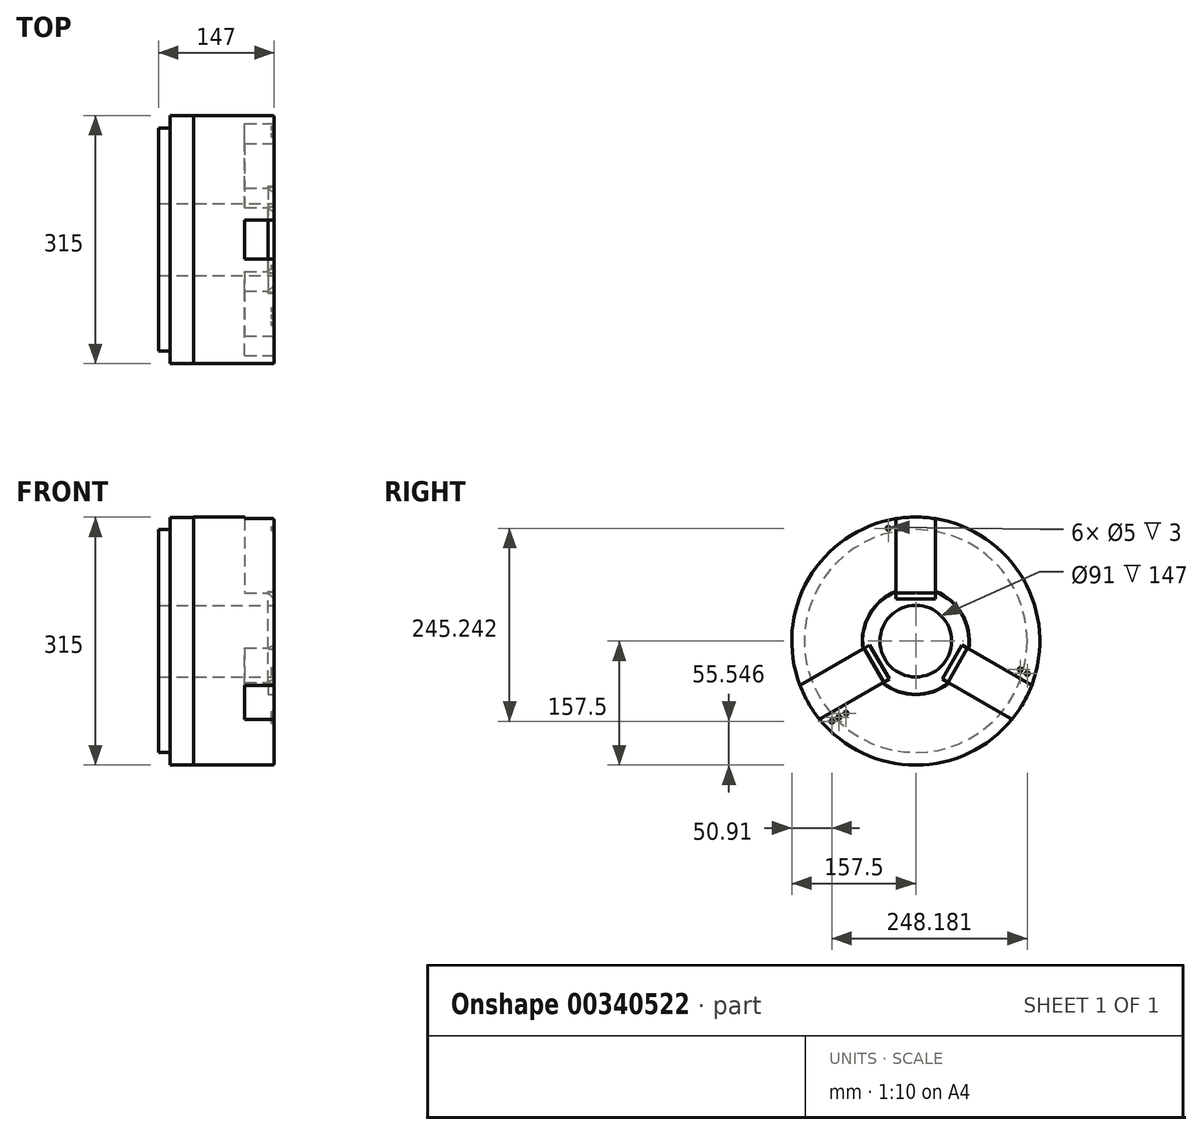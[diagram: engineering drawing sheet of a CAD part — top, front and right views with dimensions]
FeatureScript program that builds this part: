
annotation { "Feature Type Name" : "Feature", "Feature Type Description" : "" }
export const myFeature = defineFeature(function(context is Context, id is Id, definition is map)
    precondition{}
    {
        {
            var Q0;
            Q0=qCreatedBy(makeId("Front.planeOp"),FACE);
            var sketch = newSketch(context, id + "F0", { "sketchPlane" : qUnion([Q0])});
            skLineSegment(sketch, "E0", {"start": v(0, 45.5) * mm, "end": v(0, 67.5) * mm});
            skLineSegment(sketch, "E1", {"start": v(-2, 157.5) * mm, "end": v(-102, 157.5) * mm});
            skLineSegment(sketch, "E2", {"start": v(-132, 157.25) * mm, "end": v(-132, 141.5) * mm});
            skLineSegment(sketch, "E3", {"start": v(-132, 141.5) * mm, "end": v(-147, 141.5) * mm});
            skLineSegment(sketch, "E4", {"start": v(-147, 141.5) * mm, "end": v(-147, 45.5) * mm});
            skLineSegment(sketch, "E5", {"start": v(-147, 45.5) * mm, "end": v(0, 45.5) * mm});
            skLineSegment(sketch, "E6", {"start": v(294.82, 0) * mm, "end": v(-412.28, 0) * mm, "construction": true});
            skPoint(sketch, "E7.visualSharp", {"position": v(0, 157.5) * mm});
            skArc(sketch, "E7.filletArc", {"start": v(0, 155.5) * mm, "mid": v(-0.59, 156.91) * mm, "end": v(-2, 157.5) * mm});
            skLineSegment(sketch, "E8.bottom", {"start": v(0, 67.5) * mm, "end": v(-8, 67.5) * mm});
            skLineSegment(sketch, "E8.top", {"start": v(0, 68) * mm, "end": v(-8, 68) * mm});
            skLineSegment(sketch, "E8.right", {"start": v(-8, 67.5) * mm, "end": v(-8, 68) * mm});
            skLineSegment(sketch, "E9.trimOffspring", {"start": v(0, 68) * mm, "end": v(0, 155.5) * mm});
            skLineSegment(sketch, "E10", {"start": v(-132, 157.25) * mm, "end": v(-102, 157.25) * mm});
            skLineSegment(sketch, "E11", {"start": v(-102, 157.25) * mm, "end": v(-102, 157.5) * mm});
            skPoint(sketch, "E12.orphan", {"position": v(-132, 157.5) * mm});
            skSolve(sketch);
        }
        {
            var Q0;
            Q0=qSketchRegion(id+"F0",true);
            var Q1;
            Q1=sQuery(id+"F0.wireOp",EDGE,"E6");
            revolve(context, id + "F1", {"entities" : qUnion([Q0]), "axis" : qUnion([Q1]), "revolveType" : RevolveType.FULL});
        }
        {
            var Q0;
            Q0=makeQuery(id+"F1.opRevolve","SWEPT_FACE",FACE,{"disambiguationData":[OSD([sQuery(id+"F0.wireOp",EDGE,"E0")])]});
            var sketch = newSketch(context, id + "F2", { "sketchPlane" : qUnion([Q0])});
            skLineSegment(sketch, "E13", {"start": v(0, 0) * mm, "end": v(0, 187.03) * mm, "construction": true});
            skArc(sketch, "E14", {"start": v(25, 155.5) * mm, "mid": v(0, 157.5) * mm, "end": v(-25, 155.5) * mm});
            skPoint(sketch, "E15", {"position": v(0, 62.16) * mm});
            skLineSegment(sketch, "E16", {"start": v(25, 155.5) * mm, "end": v(25, 60.5) * mm});
            skLineSegment(sketch, "E17", {"start": v(25, 60.5) * mm, "end": v(-25, 60.5) * mm});
            skLineSegment(sketch, "E18", {"start": v(-25, 60.5) * mm, "end": v(-25, 155.5) * mm});
            skSolve(sketch);
        }
        {
            var Q0;
            {var subQ0=sQuery(id+"F2.wireOp",EDGE,"E14");Q0=makeQuery(id+"F2.imprint","IMPRINT",FACE,{"disambiguationData":[TD([[makeQuery(id+"F2.imprint","IMPRINT",EDGE,{"derivedFrom":subQ0}),1.0]])]});}
            var Q1;
            {var subQ0=sQuery(id+"F2.wireOp",EDGE,"LmhPQE9t-ctvD-aCPM-Uwr9-EQLkLqq6skGc.bottom");Q1=makeQuery(id+"F2.imprint","IMPRINT",FACE,{"disambiguationData":[TD([[makeQuery(id+"F2.imprint","IMPRINT",EDGE,{"derivedFrom":subQ0}),-1.0]])]});}
            var Q2;
            {var subQ0=sQuery(id+"F2.wireOp",EDGE,"LmhPQE9t-ctvD-aCPM-Uwr9-EQLkLqq6skGc.bottom");var subQ1=makeQuery(id+"F1.opRevolve","SWEPT_EDGE",EDGE,{"disambiguationData":[OSD([sQuery(id+"F0.wireOp",EDGE,"E0"),sQuery(id+"F0.wireOp",EDGE,"E8.bottom")])]});var subQ2=makeQuery(id+"F2.imprint","INTERSECT",VERTEX,{"disambiguationData":[OD(0.0)],"derivedFrom":[subQ1,subQ0]});Q2=makeQuery(id+"F2.imprint","IMPRINT",FACE,{"disambiguationData":[TD([[makeQuery(id+"F2.imprint","IMPRINT",EDGE,{"disambiguationData":[TD([[subQ2,-1.0]])],"derivedFrom":subQ0}),-1.0]])]});}
            extrude(context, id + "F3", {"entities" : qUnion([Q0, Q1, Q2]), "operationType" : NewBodyOperationType.REMOVE, "oppositeDirection" : true, "depth" : 37.5 * mm});
        }
        {
            var Q0;
            Q0=makeQuery(id+"F1.opRevolve","SWEPT_FACE",FACE,{"disambiguationData":[OSD([sQuery(id+"F0.wireOp",EDGE,"E0")])]});
            var sketch = newSketch(context, id + "F4", { "sketchPlane" : qUnion([Q0])});
            skLineSegment(sketch, "E19", {"start": v(25, 73.3) * mm, "end": v(-25, 73.3) * mm});
            skLineSegment(sketch, "E20", {"start": v(-25, 73.3) * mm, "end": v(-25, 53.3) * mm});
            skLineSegment(sketch, "E21", {"start": v(-25, 53.3) * mm, "end": v(25, 53.3) * mm});
            skLineSegment(sketch, "E22", {"start": v(25, 53.3) * mm, "end": v(25, 73.3) * mm});
            skSolve(sketch);
        }
        {
            var Q0;
            Q0=qSketchRegion(id+"F4",true);
            extrude(context, id + "F5", {"entities" : qUnion([Q0]), "operationType" : NewBodyOperationType.REMOVE, "oppositeDirection" : true, "depth" : 8 * mm});
        }
        {
            var Q0;
            Q0=makeQuery(id+"F5.boolean.opBoolean","COPY",EDGE,{"derivedFrom":makeQuery(id+"F5.opExtrude","CAP_EDGE",EDGE,{"disambiguationData":[OSD([sQuery(id+"F4.wireOp",EDGE,"E21")])],"isStart":false})});
            chamfer(context, id + "F6", {"entities" : qUnion([Q0]), "width" : 8 * mm, "tangentPropagation" : true});
        }
        {
            var Q0;
            Q0=makeQuery(id+"F5.boolean.opBoolean","COPY",FACE,{"derivedFrom":makeQuery(id+"F5.opExtrude","CAP_FACE",FACE,{"disambiguationData":[OSD([sQuery(id+"F4.wireOp",EDGE,"E19"),sQuery(id+"F4.wireOp",EDGE,"E20"),sQuery(id+"F4.wireOp",EDGE,"E21"),sQuery(id+"F4.wireOp",EDGE,"E22")])],"isStart":false})});
            var Q1;
            Q1=makeQuery(id+"F3.boolean.opBoolean","COPY",FACE,{"derivedFrom":makeQuery(id+"F3.opExtrude","CAP_FACE",FACE,{"disambiguationData":[OSD([sQuery(id+"F0.wireOp",EDGE,"E0"),sQuery(id+"F0.wireOp",EDGE,"E8.bottom"),sQuery(id+"F2.wireOp",EDGE,"E14"),sQuery(id+"F2.wireOp",EDGE,"E16"),sQuery(id+"F2.wireOp",EDGE,"E18")])],"isStart":false})});
            extrude(context, id + "F7", {"entities" : qUnion([Q0]), "operationType" : NewBodyOperationType.REMOVE, "endBound" : BoundingType.UP_TO_SURFACE, "oppositeDirection" : true, "endBoundEntityFace" : qUnion([Q1]), "depth" : 25 * mm});
        }
        {
            var Q0;
            Q0=makeQuery(id+"F6.opChamfer","BLEND_FACE",FACE,{"disambiguationData":[OSD([sQuery(id+"F4.wireOp",EDGE,"E21")])]});
            var Q1;
            {var subQ0=sQuery(id+"F4.wireOp",EDGE,"E22");Q1=makeQuery(id+"F7.boolean.opBoolean","MERGE",FACE,{"derivedFrom":[makeQuery(id+"F3.boolean.opBoolean","COPY",FACE,{"derivedFrom":makeQuery(id+"F3.opExtrude","SWEPT_FACE",FACE,{"disambiguationData":[OSD([sQuery(id+"F2.wireOp",EDGE,"E16")])]})}),makeQuery(id+"F5.boolean.opBoolean","COPY",FACE,{"derivedFrom":makeQuery(id+"F5.opExtrude","SWEPT_FACE",FACE,{"disambiguationData":[OSD([subQ0])]})}),makeQuery(id+"F7.opExtrude","SWEPT_FACE",FACE,{"disambiguationData":[OSD([subQ0])]})]});}
            var Q2;
            Q2=makeQuery(id+"F7.boolean.opBoolean","COPY",FACE,{"derivedFrom":makeQuery(id+"F7.opExtrude","SWEPT_FACE",FACE,{"disambiguationData":[OSD([sQuery(id+"F4.wireOp",EDGE,"E19"),sQuery(id+"F4.wireOp",EDGE,"E20"),sQuery(id+"F4.wireOp",EDGE,"E21"),sQuery(id+"F4.wireOp",EDGE,"E22")])]})});
            var Q3;
            {var subQ0=sQuery(id+"F2.wireOp",EDGE,"E18");var subQ1=sQuery(id+"F2.wireOp",EDGE,"E16");var subQ2=sQuery(id+"F2.wireOp",EDGE,"E14");var subQ3=sQuery(id+"F0.wireOp",EDGE,"E8.bottom");var subQ4=sQuery(id+"F0.wireOp",EDGE,"E0");Q3=makeQuery(id+"F7.boolean.opBoolean","MERGE",FACE,{"derivedFrom":[makeQuery(id+"F3.boolean.opBoolean","COPY",FACE,{"derivedFrom":makeQuery(id+"F3.opExtrude","CAP_FACE",FACE,{"disambiguationData":[OSD([subQ4,subQ3,subQ2,subQ1,subQ0])],"isStart":false})}),makeQuery(id+"F7.opExtrude","CAP_FACE",FACE,{"disambiguationData":[OSD([subQ4,subQ3,subQ2,subQ1,subQ0])],"isStart":false})]});}
            var Q4;
            {var subQ0=sQuery(id+"F4.wireOp",EDGE,"E20");Q4=makeQuery(id+"F7.boolean.opBoolean","MERGE",FACE,{"derivedFrom":[makeQuery(id+"F3.boolean.opBoolean","COPY",FACE,{"derivedFrom":makeQuery(id+"F3.opExtrude","SWEPT_FACE",FACE,{"disambiguationData":[OSD([sQuery(id+"F2.wireOp",EDGE,"E18")])]})}),makeQuery(id+"F5.boolean.opBoolean","COPY",FACE,{"derivedFrom":makeQuery(id+"F5.opExtrude","SWEPT_FACE",FACE,{"disambiguationData":[OSD([subQ0])]})}),makeQuery(id+"F7.opExtrude","SWEPT_FACE",FACE,{"disambiguationData":[OSD([subQ0])]})]});}
            var Q5;
            Q5=makeQuery(id+"F1.opRevolve","SWEPT_FACE",FACE,{"disambiguationData":[OSD([sQuery(id+"F0.wireOp",EDGE,"E5")])]});
            circularPattern(context, id + "F8", {"patternType" : PatternType.FACE, "operationType" : NewBodyOperationType.ADD, "faces" : qUnion([Q0, Q1, Q2, Q3, Q4]), "axis" : qUnion([Q5]), "angle" : 360 * degree, "instanceCount" : 3, "equalSpace" : true});
        }
        {
            var Q0;
            Q0=makeQuery(id+"F1.opRevolve","SWEPT_FACE",FACE,{"disambiguationData":[OSD([sQuery(id+"F0.wireOp",EDGE,"E0")])]});
            var sketch = newSketch(context, id + "F9", { "sketchPlane" : qUnion([Q0])});
            skCircle(sketch, "E23", {"center": v(-35, 143.29) * mm, "radius": 2.5 * mm});
            skCircle(sketch, "E24", {"center": v(0, 0) * mm, "radius": 147.5 * mm, "construction": true});
            skCircle(sketch, "E25", {"center": v(0, 0) * mm, "radius": 137.5 * mm, "construction": true});
            skCircle(sketch, "E26", {"center": v(0, 0) * mm, "radius": 127.5 * mm, "construction": true});
            skCircle(sketch, "E27", {"center": v(141.6, -41.33) * mm, "radius": 2.5 * mm});
            skCircle(sketch, "E28", {"center": v(132.66, -36.17) * mm, "radius": 2.5 * mm});
            skCircle(sketch, "E29", {"center": v(-106.6, -101.95) * mm, "radius": 2.5 * mm});
            skCircle(sketch, "E30", {"center": v(-97.66, -96.8) * mm, "radius": 2.5 * mm});
            skCircle(sketch, "E31", {"center": v(-88.68, -91.61) * mm, "radius": 2.5 * mm});
            skLineSegment(sketch, "E32", {"start": v(-35, 143.29) * mm, "end": v(-35, 107.8) * mm, "construction": true});
            skLineSegment(sketch, "E33", {"start": v(0, 107.8) * mm, "end": v(0, 150.74) * mm, "construction": true});
            skCircle(sketch, "E34.MirrorC", {"center": v(35, 143.29) * mm, "radius": 2.5 * mm});
            skLineSegment(sketch, "E35", {"start": v(141.6, -41.33) * mm, "end": v(110.08, -23.14) * mm, "construction": true});
            skLineSegment(sketch, "E36", {"start": v(0, 0) * mm, "end": v(131.49, -75.91) * mm, "construction": true});
            skCircle(sketch, "E37.MirrorC", {"center": v(97.66, -96.8) * mm, "radius": 2.5 * mm});
            skCircle(sketch, "E38.MirrorC", {"center": v(106.6, -101.95) * mm, "radius": 2.5 * mm});
            skLineSegment(sketch, "E39", {"start": v(0, 0) * mm, "end": v(-132.86, -76.7) * mm, "construction": true});
            skLineSegment(sketch, "E40", {"start": v(-106.6, -101.95) * mm, "end": v(-83.53, -88.64) * mm, "construction": true});
            skCircle(sketch, "E41.MirrorC", {"center": v(-123.68, -31) * mm, "radius": 2.5 * mm});
            skCircle(sketch, "E42.MirrorC", {"center": v(-132.66, -36.17) * mm, "radius": 2.5 * mm});
            skCircle(sketch, "E43.MirrorC", {"center": v(-141.6, -41.33) * mm, "radius": 2.5 * mm});
            skSolve(sketch);
        }
        {
            var Q0;
            Q0=makeQuery(id+"F9.imprint","IMPRINT",FACE,{"disambiguationData":[TD([[makeQuery(id+"F9.imprint","IMPRINT",EDGE,{"derivedFrom":sQuery(id+"F9.wireOp",EDGE,"E43.MirrorC")}),-1.0]])]});
            var Q1;
            Q1=makeQuery(id+"F9.imprint","IMPRINT",FACE,{"disambiguationData":[TD([[makeQuery(id+"F9.imprint","IMPRINT",EDGE,{"derivedFrom":sQuery(id+"F9.wireOp",EDGE,"E42.MirrorC")}),-1.0]])]});
            var Q2;
            Q2=makeQuery(id+"F9.imprint","IMPRINT",FACE,{"disambiguationData":[TD([[makeQuery(id+"F9.imprint","IMPRINT",EDGE,{"derivedFrom":sQuery(id+"F9.wireOp",EDGE,"E41.MirrorC")}),-1.0]])]});
            var Q3;
            Q3=makeQuery(id+"F9.imprint","IMPRINT",FACE,{"disambiguationData":[TD([[makeQuery(id+"F9.imprint","IMPRINT",EDGE,{"derivedFrom":sQuery(id+"F9.wireOp",EDGE,"E31")}),1.0]])]});
            var Q4;
            Q4=makeQuery(id+"F9.imprint","IMPRINT",FACE,{"disambiguationData":[TD([[makeQuery(id+"F9.imprint","IMPRINT",EDGE,{"derivedFrom":sQuery(id+"F9.wireOp",EDGE,"E30")}),1.0]])]});
            var Q5;
            Q5=makeQuery(id+"F9.imprint","IMPRINT",FACE,{"disambiguationData":[TD([[makeQuery(id+"F9.imprint","IMPRINT",EDGE,{"derivedFrom":sQuery(id+"F9.wireOp",EDGE,"E29")}),1.0]])]});
            var Q6;
            Q6=makeQuery(id+"F9.imprint","IMPRINT",FACE,{"disambiguationData":[TD([[makeQuery(id+"F9.imprint","IMPRINT",EDGE,{"derivedFrom":sQuery(id+"F9.wireOp",EDGE,"E37.MirrorC")}),-1.0]])]});
            var Q7;
            Q7=makeQuery(id+"F9.imprint","IMPRINT",FACE,{"disambiguationData":[TD([[makeQuery(id+"F9.imprint","IMPRINT",EDGE,{"derivedFrom":sQuery(id+"F9.wireOp",EDGE,"E38.MirrorC")}),-1.0]])]});
            var Q8;
            Q8=makeQuery(id+"F9.imprint","IMPRINT",FACE,{"disambiguationData":[TD([[makeQuery(id+"F9.imprint","IMPRINT",EDGE,{"derivedFrom":sQuery(id+"F9.wireOp",EDGE,"E27")}),1.0]])]});
            var Q9;
            Q9=makeQuery(id+"F9.imprint","IMPRINT",FACE,{"disambiguationData":[TD([[makeQuery(id+"F9.imprint","IMPRINT",EDGE,{"derivedFrom":sQuery(id+"F9.wireOp",EDGE,"E28")}),1.0]])]});
            var Q10;
            Q10=makeQuery(id+"F9.imprint","IMPRINT",FACE,{"disambiguationData":[TD([[makeQuery(id+"F9.imprint","IMPRINT",EDGE,{"derivedFrom":sQuery(id+"F9.wireOp",EDGE,"E34.MirrorC")}),-1.0]])]});
            var Q11;
            Q11=makeQuery(id+"F9.imprint","IMPRINT",FACE,{"disambiguationData":[TD([[makeQuery(id+"F9.imprint","IMPRINT",EDGE,{"derivedFrom":sQuery(id+"F9.wireOp",EDGE,"E23")}),1.0]])]});
            var Q12;
            Q12=sQuery(id+"F9.wireOp",EDGE,"E23");
            var Q13;
            Q13=sQuery(id+"F9.wireOp",EDGE,"E34.MirrorC");
            var Q14;
            Q14=sQuery(id+"F9.wireOp",EDGE,"E28");
            var Q15;
            Q15=sQuery(id+"F9.wireOp",EDGE,"E27");
            var Q16;
            Q16=sQuery(id+"F9.wireOp",EDGE,"E38.MirrorC");
            var Q17;
            Q17=sQuery(id+"F9.wireOp",EDGE,"E37.MirrorC");
            var Q18;
            Q18=sQuery(id+"F9.wireOp",EDGE,"E31");
            var Q19;
            Q19=sQuery(id+"F9.wireOp",EDGE,"E30");
            var Q20;
            Q20=sQuery(id+"F9.wireOp",EDGE,"E29");
            var Q21;
            Q21=sQuery(id+"F9.wireOp",EDGE,"E41.MirrorC");
            var Q22;
            Q22=sQuery(id+"F9.wireOp",EDGE,"E42.MirrorC");
            var Q23;
            Q23=sQuery(id+"F9.wireOp",EDGE,"E43.MirrorC");
            extrude(context, id + "F10", {"entities" : qUnion([Q0, Q1, Q2, Q3, Q4, Q5, Q6, Q7, Q8, Q9, Q10, Q11]), "operationType" : NewBodyOperationType.REMOVE, "surfaceEntities" : qUnion([Q12, Q13, Q14, Q15, Q16, Q17, Q18, Q19, Q20, Q21, Q22, Q23]), "oppositeDirection" : true, "depth" : 3 * mm});
        }
    });
